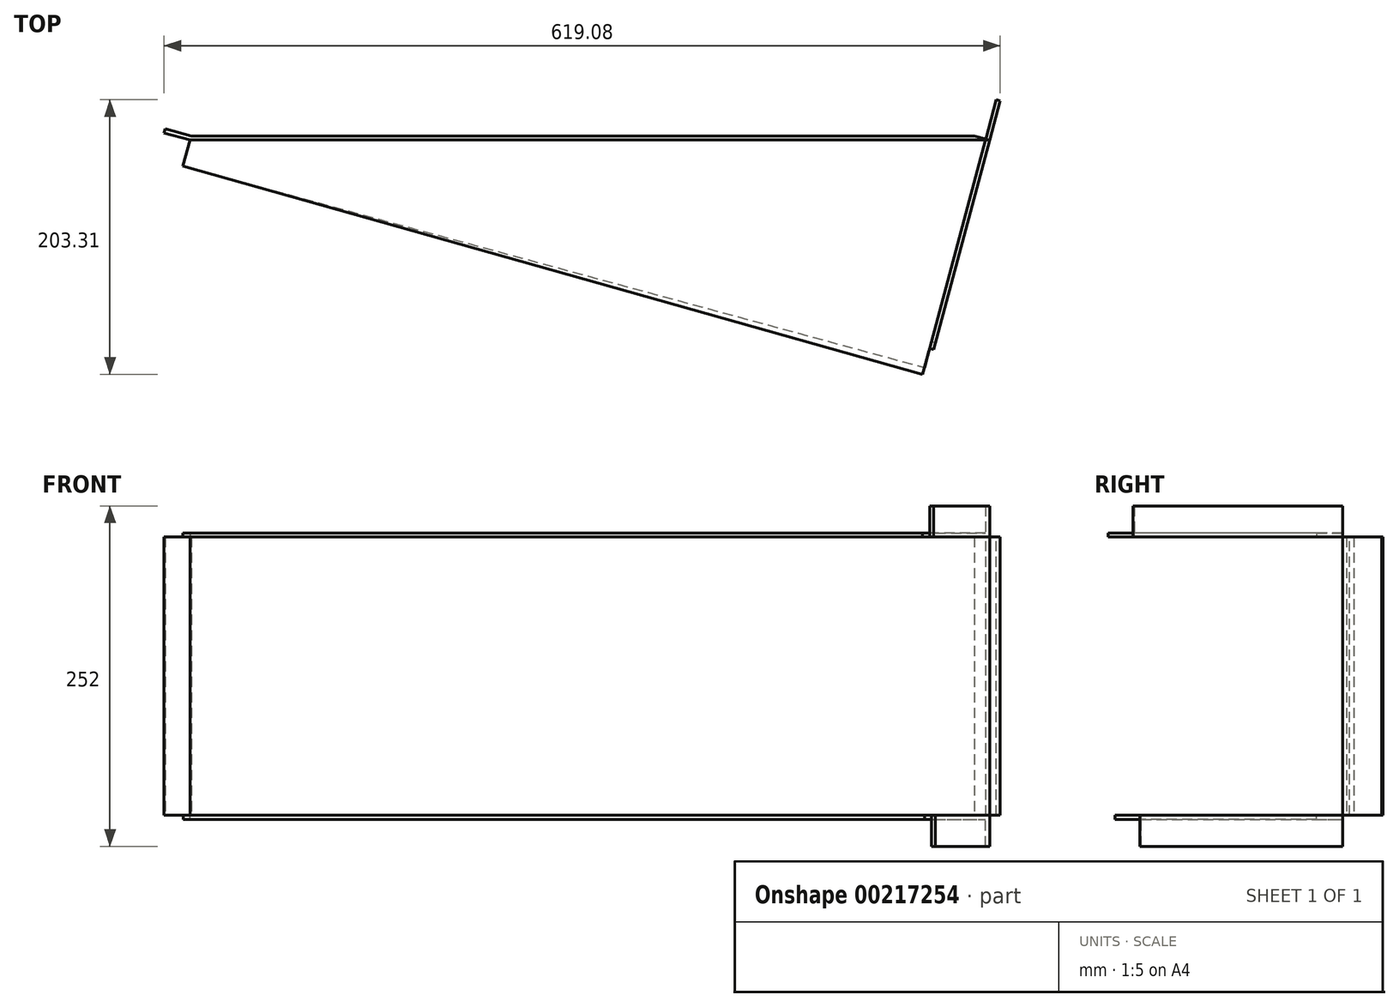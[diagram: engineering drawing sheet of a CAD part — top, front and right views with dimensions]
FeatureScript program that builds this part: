
annotation { "Feature Type Name" : "Feature", "Feature Type Description" : "" }
export const myFeature = defineFeature(function(context is Context, id is Id, definition is map)
    precondition{}
    {
        {
            var Q0;
            Q0=qCreatedBy(makeId("Front.planeOp"),FACE);
            var sketch = newSketch(context, id + "F0", { "sketchPlane" : qUnion([Q0])});
            skLineSegment(sketch, "E0.bottom", {"start": v(-290, 103) * mm, "end": v(290, 103) * mm});
            skLineSegment(sketch, "E0.top", {"start": v(-290, -103) * mm, "end": v(290, -103) * mm});
            skLineSegment(sketch, "E0.left", {"start": v(-290, 103) * mm, "end": v(-290, -103) * mm});
            skLineSegment(sketch, "E0.right", {"start": v(290, 103) * mm, "end": v(290, -103) * mm});
            skPoint(sketch, "E0.middle", {"position": v(0, 0) * mm});
            skSolve(sketch);
        }
        {
            var Q0;
            Q0 = qSketchRegion(id + "F0", true);
            extrude(context, id + "F1", {"entities" : qUnion([Q0]), "depth" : 3 * mm});
        }
        {
            var Q0;
            Q0=makeQuery(id+"F1.opExtrude","SWEPT_FACE",FACE,{"disambiguationData":[OSD([sQuery(id+"F0.wireOp",EDGE,"E0.bottom")])]});
            var sketch = newSketch(context, id + "F2", { "sketchPlane" : qUnion([Q0])});
            skLineSegment(sketch, "E1", {"start": v(-290, 0) * mm, "end": v(-290.8, -3) * mm});
            skLineSegment(sketch, "E2", {"start": v(-290, -3) * mm, "end": v(-290.8, -3) * mm});
            skLineSegment(sketch, "E3", {"start": v(290, 0) * mm, "end": v(301.2, -3) * mm});
            skLineSegment(sketch, "E4", {"start": v(290, -3) * mm, "end": v(301.2, -3) * mm});
            skLineSegment(sketch, "E5", {"start": v(-290.8, -3) * mm, "end": v(259.63, -158.12) * mm});
            skLineSegment(sketch, "E6", {"start": v(301.2, -3) * mm, "end": v(259.63, -158.12) * mm});
            skSolve(sketch);
        }
        {
            var Q0;
            Q0=makeQuery(id+"F2.imprint","IMPRINT",FACE,{"disambiguationData":[TD([[makeQuery(id+"F2.imprint","IMPRINT",EDGE,{"derivedFrom":sQuery(id+"F2.wireOp",EDGE,"E1")}),1.0]])]});
            extrude(context, id + "F3", {"entities" : qUnion([Q0]), "operationType" : NewBodyOperationType.ADD, "oppositeDirection" : true, "depth" : 206 * mm});
        }
        {
            var Q0;
            Q0=makeQuery(id+"F3.opExtrude","SWEPT_FACE",FACE,{"disambiguationData":[OSD([sQuery(id+"F2.wireOp",EDGE,"E1")])]});
            var sketch = newSketch(context, id + "F4", { "sketchPlane" : qUnion([Q0])});
            skLineSegment(sketch, "E7.bottom", {"start": v(75.06, 103) * mm, "end": v(78.16, 103) * mm});
            skLineSegment(sketch, "E7.top", {"start": v(75.06, -103) * mm, "end": v(78.16, -103) * mm});
            skLineSegment(sketch, "E7.left", {"start": v(75.06, 103) * mm, "end": v(75.06, -103) * mm});
            skLineSegment(sketch, "E7.right", {"start": v(78.16, 103) * mm, "end": v(78.16, -103) * mm});
            skSolve(sketch);
        }
        {
            var Q0;
            Q0=makeQuery(id+"F4.imprint","IMPRINT",FACE,{"disambiguationData":[TD([[makeQuery(id+"F4.imprint","IMPRINT",EDGE,{"derivedFrom":sQuery(id+"F4.wireOp",EDGE,"E7.bottom")}),-1.0]])]});
            extrude(context, id + "F5", {"entities" : qUnion([Q0]), "operationType" : NewBodyOperationType.ADD, "depth" : 20 * mm});
        }
        {
            var Q0;
            Q0=makeQuery(id+"F2.imprint","IMPRINT",FACE,{"disambiguationData":[TD([[makeQuery(id+"F2.imprint","IMPRINT",EDGE,{"derivedFrom":sQuery(id+"F2.wireOp",EDGE,"E3")}),-1.0]])]});
            extrude(context, id + "F6", {"entities" : qUnion([Q0]), "operationType" : NewBodyOperationType.ADD, "oppositeDirection" : true, "depth" : 206 * mm});
        }
        {
            var Q0;
            Q0=makeQuery(id+"F6.opExtrude","SWEPT_FACE",FACE,{"disambiguationData":[OSD([sQuery(id+"F2.wireOp",EDGE,"E3")])]});
            var sketch = newSketch(context, id + "F7", { "sketchPlane" : qUnion([Q0])});
            skLineSegment(sketch, "E8.right", {"start": v(-291.7, 103) * mm, "end": v(-291.7, -103) * mm});
            skLineSegment(sketch, "E9", {"start": v(-291.7, -103) * mm, "end": v(-288.7, -103) * mm});
            skLineSegment(sketch, "E10", {"start": v(-288.7, -103) * mm, "end": v(-288.7, 103) * mm});
            skLineSegment(sketch, "E11", {"start": v(-288.7, 103) * mm, "end": v(-291.7, 103) * mm});
            skSolve(sketch);
        }
        {
            var Q0;
            Q0=makeQuery(id+"F7.imprint","IMPRINT",FACE,{"disambiguationData":[TD([[makeQuery(id+"F7.imprint","IMPRINT",EDGE,{"derivedFrom":sQuery(id+"F7.wireOp",EDGE,"E8.bottom")}),1.0]])]});
            var Q1;
            Q1=makeQuery(id+"F7.imprint","IMPRINT",FACE,{"disambiguationData":[TD([[makeQuery(id+"F7.imprint","IMPRINT",EDGE,{"derivedFrom":sQuery(id+"F7.wireOp",EDGE,"E8.right")}),-1.0]])]});
            extrude(context, id + "F8", {"entities" : qUnion([Q0, Q1]), "operationType" : NewBodyOperationType.ADD, "depth" : 30 * mm});
        }
        {
            var Q0;
            Q0=makeQuery(id+"F2.imprint","IMPRINT",FACE,{"disambiguationData":[TD([[makeQuery(id+"F2.imprint","IMPRINT",EDGE,{"derivedFrom":sQuery(id+"F2.wireOp",EDGE,"E2")}),1.0]])]});
            extrude(context, id + "F9", {"entities" : qUnion([Q0]), "depth" : 3 * mm});
        }
        {
            var Q0;
            {var subQ0=sQuery(id+"F0.wireOp",EDGE,"E0.bottom");Q0=makeQuery(id+"F8.boolean.opBoolean","MERGE",FACE,{"derivedFrom":[makeQuery(id+"F6.boolean.opBoolean","MERGE",FACE,{"derivedFrom":[makeQuery(id+"F5.boolean.opBoolean","MERGE",FACE,{"derivedFrom":[makeQuery(id+"F3.boolean.opBoolean","MERGE",FACE,{"derivedFrom":[makeQuery(id+"F1.opExtrude","SWEPT_FACE",FACE,{"disambiguationData":[OSD([sQuery(id+"F0.wireOp",EDGE,"E0.top")])]}),makeQuery(id+"F3.opExtrude","CAP_FACE",FACE,{"disambiguationData":[OSD([subQ0,sQuery(id+"F0.wireOp",EDGE,"E0.left"),sQuery(id+"F2.wireOp",EDGE,"E1"),sQuery(id+"F2.wireOp",EDGE,"E2")])],"isStart":false})]}),makeQuery(id+"F5.opExtrude","SWEPT_FACE",FACE,{"disambiguationData":[OSD([sQuery(id+"F4.wireOp",EDGE,"E7.top")])]})]}),makeQuery(id+"F6.opExtrude","CAP_FACE",FACE,{"disambiguationData":[OSD([subQ0,sQuery(id+"F0.wireOp",EDGE,"E0.right"),sQuery(id+"F2.wireOp",EDGE,"E3"),sQuery(id+"F2.wireOp",EDGE,"E4")])],"isStart":false})]}),makeQuery(id+"F8.opExtrude","SWEPT_FACE",FACE,{"disambiguationData":[OSD([sQuery(id+"F7.wireOp",EDGE,"E9")])]})]});}
            var sketch = newSketch(context, id + "F10", { "sketchPlane" : qUnion([Q0])});
            skLineSegment(sketch, "E12", {"start": v(-290.8, 3) * mm, "end": v(261, 152.98) * mm});
            skLineSegment(sketch, "E13", {"start": v(261, 152.98) * mm, "end": v(301.2, 3) * mm});
            skSolve(sketch);
        }
        {
            var Q0;
            Q0=makeQuery(id+"F10.imprint","IMPRINT",FACE,{"disambiguationData":[TD([[makeQuery(id+"F10.imprint","IMPRINT",EDGE,{"derivedFrom":sQuery(id+"F10.wireOp",EDGE,"E12")}),-1.0]])]});
            extrude(context, id + "F11", {"entities" : qUnion([Q0]), "depth" : 3 * mm});
        }
        {
            var Q0;
            Q0=makeQuery(id+"F11.opExtrude","CAP_FACE",FACE,{"disambiguationData":[OSD([sQuery(id+"F0.wireOp",EDGE,"E0.top"),sQuery(id+"F2.wireOp",EDGE,"E2"),sQuery(id+"F2.wireOp",EDGE,"E4"),sQuery(id+"F10.wireOp",EDGE,"E12"),sQuery(id+"F10.wireOp",EDGE,"E13")])],"isStart":false});
            var sketch = newSketch(context, id + "F12", { "sketchPlane" : qUnion([Q0])});
            skLineSegment(sketch, "E14", {"start": v(261, 152.98) * mm, "end": v(301.2, 3) * mm});
            skLineSegment(sketch, "E15", {"start": v(301.2, 3) * mm, "end": v(298.1, 3) * mm});
            skLineSegment(sketch, "E16", {"start": v(261, 152.98) * mm, "end": v(258.11, 152.2) * mm});
            skLineSegment(sketch, "E17", {"start": v(258.11, 152.2) * mm, "end": v(298.1, 3) * mm});
            skSolve(sketch);
        }
        {
            var Q0;
            Q0=makeQuery(id+"F12.imprint","IMPRINT",FACE,{"disambiguationData":[TD([[makeQuery(id+"F12.imprint","IMPRINT",EDGE,{"derivedFrom":sQuery(id+"F12.wireOp",EDGE,"E14")}),-1.0]])]});
            extrude(context, id + "F13", {"entities" : qUnion([Q0]), "operationType" : NewBodyOperationType.ADD, "depth" : 20 * mm});
        }
        {
            var Q0;
            Q0=makeQuery(id+"F9.opExtrude","CAP_FACE",FACE,{"disambiguationData":[OSD([sQuery(id+"F0.wireOp",EDGE,"E0.bottom"),sQuery(id+"F2.wireOp",EDGE,"E2"),sQuery(id+"F2.wireOp",EDGE,"E4"),sQuery(id+"F2.wireOp",EDGE,"E5"),sQuery(id+"F2.wireOp",EDGE,"E6")])],"isStart":false});
            var sketch = newSketch(context, id + "F14", { "sketchPlane" : qUnion([Q0])});
            skLineSegment(sketch, "E18", {"start": v(259.63, -158.12) * mm, "end": v(256.74, -157.3) * mm});
            skLineSegment(sketch, "E19", {"start": v(259.63, -158.12) * mm, "end": v(301.2, -3) * mm});
            skLineSegment(sketch, "E20", {"start": v(301.2, -3) * mm, "end": v(298.1, -3) * mm});
            skLineSegment(sketch, "E21", {"start": v(298.1, -3) * mm, "end": v(256.74, -157.3) * mm});
            skSolve(sketch);
        }
        {
            var Q0;
            Q0=makeQuery(id+"F14.imprint","IMPRINT",FACE,{"disambiguationData":[TD([[makeQuery(id+"F14.imprint","IMPRINT",EDGE,{"derivedFrom":sQuery(id+"F14.wireOp",EDGE,"E18")}),1.0]])]});
            extrude(context, id + "F15", {"entities" : qUnion([Q0]), "operationType" : NewBodyOperationType.ADD, "depth" : 20 * mm});
        }
        {
            var Q0;
            Q0=makeQuery(id+"F13.boolean.opBoolean","MERGE",FACE,{"derivedFrom":[makeQuery(id+"F11.opExtrude","SWEPT_FACE",FACE,{"disambiguationData":[OSD([sQuery(id+"F10.wireOp",EDGE,"E12")])]}),makeQuery(id+"F13.opExtrude","SWEPT_FACE",FACE,{"disambiguationData":[OSD([sQuery(id+"F12.wireOp",EDGE,"E16")])]})]});
            var sketch = newSketch(context, id + "F16", { "sketchPlane" : qUnion([Q0])});
            skLineSegment(sketch, "E22.bottom", {"start": v(-279.84, -106) * mm, "end": v(289, -106) * mm});
            skLineSegment(sketch, "E22.top", {"start": v(-279.84, -103) * mm, "end": v(289, -103) * mm});
            skLineSegment(sketch, "E22.left", {"start": v(-279.84, -106) * mm, "end": v(-279.84, -103) * mm});
            skLineSegment(sketch, "E22.right", {"start": v(289, -106) * mm, "end": v(289, -103) * mm});
            skSolve(sketch);
        }
        {
            var Q0;
            Q0=makeQuery(id+"F16.imprint","IMPRINT",FACE,{"disambiguationData":[TD([[makeQuery(id+"F16.imprint","IMPRINT",EDGE,{"derivedFrom":sQuery(id+"F16.wireOp",EDGE,"E22.bottom")}),1.0]])]});
            extrude(context, id + "F17", {"entities" : qUnion([Q0]), "operationType" : NewBodyOperationType.ADD, "depth" : 20 * mm});
        }
        {
            var Q0;
            Q0=makeQuery(id+"F15.boolean.opBoolean","MERGE",FACE,{"derivedFrom":[makeQuery(id+"F9.opExtrude","SWEPT_FACE",FACE,{"disambiguationData":[OSD([sQuery(id+"F2.wireOp",EDGE,"E5")])]}),makeQuery(id+"F15.opExtrude","SWEPT_FACE",FACE,{"disambiguationData":[OSD([sQuery(id+"F14.wireOp",EDGE,"E18")])]})]});
            var sketch = newSketch(context, id + "F18", { "sketchPlane" : qUnion([Q0])});
            skLineSegment(sketch, "E23.bottom", {"start": v(-279.09, 103) * mm, "end": v(289.79, 103) * mm});
            skLineSegment(sketch, "E23.top", {"start": v(-279.09, 106) * mm, "end": v(289.79, 106) * mm});
            skLineSegment(sketch, "E23.left", {"start": v(-279.09, 103) * mm, "end": v(-279.09, 106) * mm});
            skLineSegment(sketch, "E23.right", {"start": v(289.79, 103) * mm, "end": v(289.79, 106) * mm});
            skSolve(sketch);
        }
        {
            var Q0;
            Q0=makeQuery(id+"F18.imprint","IMPRINT",FACE,{"disambiguationData":[TD([[makeQuery(id+"F18.imprint","IMPRINT",EDGE,{"derivedFrom":sQuery(id+"F18.wireOp",EDGE,"E23.bottom")}),1.0]])]});
            extrude(context, id + "F19", {"entities" : qUnion([Q0]), "operationType" : NewBodyOperationType.ADD, "depth" : 20 * mm});
        }
    });
